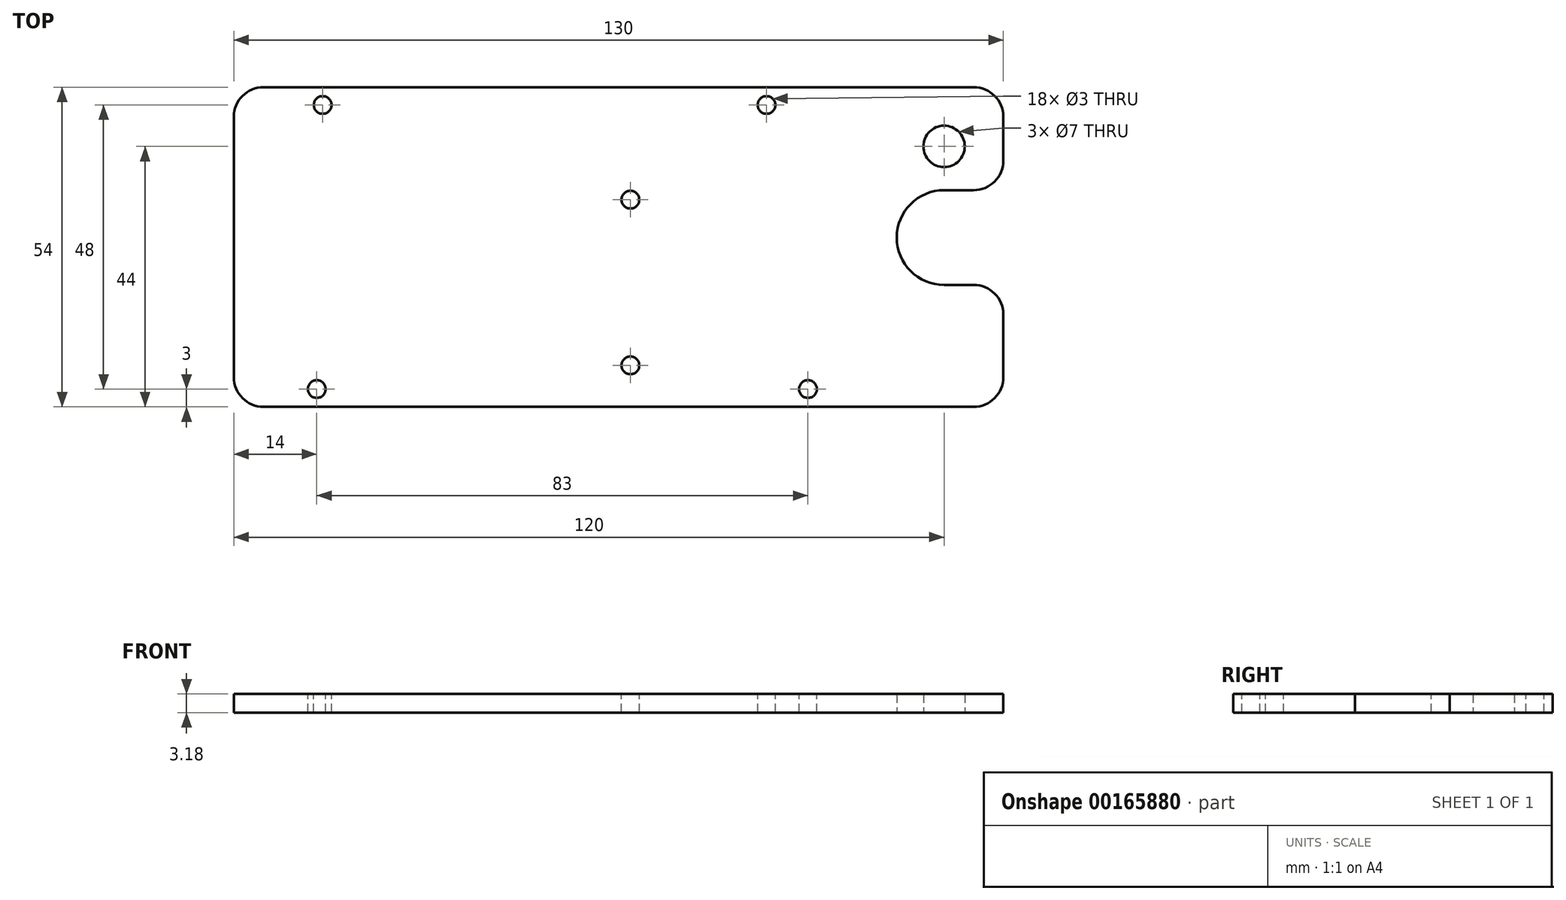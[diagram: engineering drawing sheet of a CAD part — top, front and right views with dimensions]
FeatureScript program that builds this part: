
annotation { "Feature Type Name" : "Feature", "Feature Type Description" : "" }
export const myFeature = defineFeature(function(context is Context, id is Id, definition is map)
    precondition{}
    {
        {
            var Q0;
            Q0=qCreatedBy(makeId("Top.planeOp"),FACE);
            var sketch = newSketch(context, id + "F0", { "sketchPlane" : qUnion([Q0])});
            skLineSegment(sketch, "E0.bottom", {"start": v(-65, 27) * mm, "end": v(65, 27) * mm});
            skLineSegment(sketch, "E0.top", {"start": v(-65, -27) * mm, "end": v(65, -27) * mm});
            skLineSegment(sketch, "E0.left", {"start": v(-65, 27) * mm, "end": v(-65, -27) * mm});
            skLineSegment(sketch, "E0.right", {"start": v(65, 27) * mm, "end": v(65, -27) * mm});
            skPoint(sketch, "E0.middle", {"position": v(0, 0) * mm});
            skCircle(sketch, "E1", {"center": v(55, 17) * mm, "radius": 3.5 * mm});
            skCircle(sketch, "E2", {"center": v(55, 1.6) * mm, "radius": 8 * mm});
            skLineSegment(sketch, "E3.bottom", {"start": v(55, 9.6) * mm, "end": v(65, 9.6) * mm});
            skLineSegment(sketch, "E3.top", {"start": v(55, -6.4) * mm, "end": v(65, -6.4) * mm});
            skLineSegment(sketch, "E3.left", {"start": v(55, 9.6) * mm, "end": v(55, -6.4) * mm});
            skLineSegment(sketch, "E3.right", {"start": v(65, 9.6) * mm, "end": v(65, -6.4) * mm});
            skSolve(sketch);
        }
        {
            var Q0;
            Q0=makeQuery(id+"F0.imprint","IMPRINT",FACE,{"disambiguationData":[TD([[makeQuery(id+"F0.imprint","IMPRINT",EDGE,{"derivedFrom":sQuery(id+"F0.wireOp",EDGE,"E0.bottom")}),-1.0]])]});
            extrude(context, id + "F1", {"entities" : qUnion([Q0]), "depth" : 3.17 * mm});
        }
        {
            var Q0;
            Q0=makeQuery(id+"F1.opExtrude","CAP_FACE",FACE,{"disambiguationData":[OSD([sQuery(id+"F0.wireOp",EDGE,"E0.bottom"),sQuery(id+"F0.wireOp",EDGE,"E0.top"),sQuery(id+"F0.wireOp",EDGE,"E0.left"),sQuery(id+"F0.wireOp",EDGE,"E0.right"),sQuery(id+"F0.wireOp",EDGE,"E1"),sQuery(id+"F0.wireOp",EDGE,"E2"),sQuery(id+"F0.wireOp",EDGE,"E3.bottom"),sQuery(id+"F0.wireOp",EDGE,"E3.top")])],"isStart":false});
            var sketch = newSketch(context, id + "F2", { "sketchPlane" : qUnion([Q0])});
            skCircle(sketch, "E4", {"center": v(25, 24) * mm, "radius": 1.5 * mm});
            skCircle(sketch, "E5", {"center": v(-50, 24) * mm, "radius": 1.5 * mm});
            skCircle(sketch, "E6", {"center": v(2, 8) * mm, "radius": 1.5 * mm});
            skCircle(sketch, "E7", {"center": v(-51, -24) * mm, "radius": 1.5 * mm});
            skCircle(sketch, "E8", {"center": v(2, -20) * mm, "radius": 1.5 * mm});
            skCircle(sketch, "E9", {"center": v(32, -24) * mm, "radius": 1.5 * mm});
            skSolve(sketch);
        }
        {
            var Q0;
            Q0=makeQuery(id+"F1.opExtrude","SWEPT_EDGE",EDGE,{"disambiguationData":[OSD([sQuery(id+"F0.wireOp",EDGE,"E0.top"),sQuery(id+"F0.wireOp",EDGE,"E0.left")])]});
            var Q1;
            Q1=makeQuery(id+"F1.opExtrude","SWEPT_EDGE",EDGE,{"disambiguationData":[OSD([sQuery(id+"F0.wireOp",EDGE,"E0.bottom"),sQuery(id+"F0.wireOp",EDGE,"E0.left")])]});
            var Q2;
            Q2=makeQuery(id+"F1.opExtrude","SWEPT_EDGE",EDGE,{"disambiguationData":[OSD([sQuery(id+"F0.wireOp",EDGE,"E0.top"),sQuery(id+"F0.wireOp",EDGE,"E0.right")])]});
            var Q3;
            Q3=makeQuery(id+"F1.opExtrude","SWEPT_EDGE",EDGE,{"disambiguationData":[OSD([sQuery(id+"F0.wireOp",EDGE,"E0.right"),sQuery(id+"F0.wireOp",EDGE,"E3.top"),sQuery(id+"F0.wireOp",EDGE,"E3.right")])]});
            var Q4;
            Q4=makeQuery(id+"F1.opExtrude","SWEPT_EDGE",EDGE,{"disambiguationData":[OSD([sQuery(id+"F0.wireOp",EDGE,"E0.right"),sQuery(id+"F0.wireOp",EDGE,"E3.bottom"),sQuery(id+"F0.wireOp",EDGE,"E3.right")])]});
            var Q5;
            Q5=makeQuery(id+"F1.opExtrude","SWEPT_EDGE",EDGE,{"disambiguationData":[OSD([sQuery(id+"F0.wireOp",EDGE,"E0.bottom"),sQuery(id+"F0.wireOp",EDGE,"E0.right")])]});
            fillet(context, id + "F3", {"entities" : qUnion([Q0, Q1, Q2, Q3, Q4, Q5]), "radius" : 5 * mm, "tangentPropagation" : true, "allowEdgeOverflow" : false});
        }
        {
            var Q0;
            Q0=makeQuery(id+"F2.imprint","IMPRINT",FACE,{"disambiguationData":[TD([[makeQuery(id+"F2.imprint","IMPRINT",EDGE,{"derivedFrom":sQuery(id+"F2.wireOp",EDGE,"E4")}),1.0]])]});
            var Q1;
            Q1=makeQuery(id+"F2.imprint","IMPRINT",FACE,{"disambiguationData":[TD([[makeQuery(id+"F2.imprint","IMPRINT",EDGE,{"derivedFrom":sQuery(id+"F2.wireOp",EDGE,"E6")}),1.0]])]});
            var Q2;
            Q2=makeQuery(id+"F2.imprint","IMPRINT",FACE,{"disambiguationData":[TD([[makeQuery(id+"F2.imprint","IMPRINT",EDGE,{"derivedFrom":sQuery(id+"F2.wireOp",EDGE,"E9")}),1.0]])]});
            var Q3;
            Q3=makeQuery(id+"F2.imprint","IMPRINT",FACE,{"disambiguationData":[TD([[makeQuery(id+"F2.imprint","IMPRINT",EDGE,{"derivedFrom":sQuery(id+"F2.wireOp",EDGE,"E8")}),1.0]])]});
            var Q4;
            Q4=makeQuery(id+"F2.imprint","IMPRINT",FACE,{"disambiguationData":[TD([[makeQuery(id+"F2.imprint","IMPRINT",EDGE,{"derivedFrom":sQuery(id+"F2.wireOp",EDGE,"E5")}),1.0]])]});
            var Q5;
            Q5=makeQuery(id+"F2.imprint","IMPRINT",FACE,{"disambiguationData":[TD([[makeQuery(id+"F2.imprint","IMPRINT",EDGE,{"derivedFrom":sQuery(id+"F2.wireOp",EDGE,"E7")}),1.0]])]});
            extrude(context, id + "F4", {"entities" : qUnion([Q0, Q1, Q2, Q3, Q4, Q5]), "operationType" : NewBodyOperationType.REMOVE, "oppositeDirection" : true, "depth" : 25 * mm});
        }
    });
